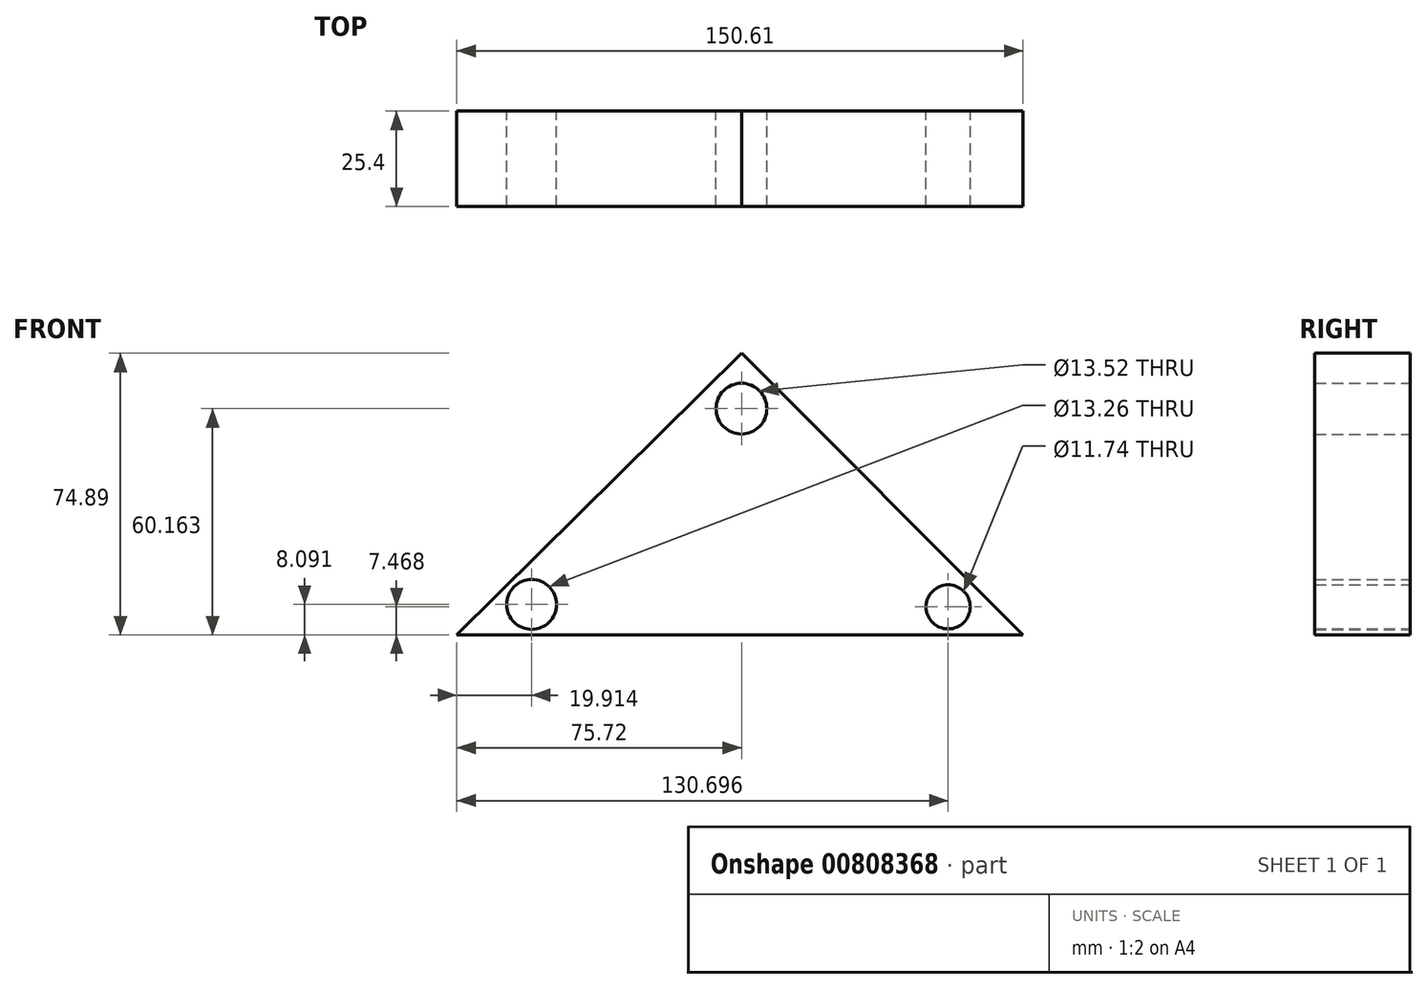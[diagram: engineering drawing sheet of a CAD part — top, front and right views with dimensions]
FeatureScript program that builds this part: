
annotation { "Feature Type Name" : "Feature", "Feature Type Description" : "" }
export const myFeature = defineFeature(function(context is Context, id is Id, definition is map)
    precondition{}
    {
        {
            var Q0;
            Q0=qCreatedBy(makeId("Front.planeOp"),FACE);
            var sketch = newSketch(context, id + "F0", { "sketchPlane" : qUnion([Q0])});
            skLineSegment(sketch, "E0", {"start": v(-75.72, 0) * mm, "end": v(74.9, 0) * mm});
            skLineSegment(sketch, "E1", {"start": v(74.9, 0) * mm, "end": v(0, 74.9) * mm});
            skLineSegment(sketch, "E2", {"start": v(0, 74.9) * mm, "end": v(-75.72, 0) * mm});
            skCircle(sketch, "E3", {"center": v(0, 60.16) * mm, "radius": 6.76 * mm});
            skCircle(sketch, "E4", {"center": v(-55.8, 8.1) * mm, "radius": 6.63 * mm});
            skCircle(sketch, "E5", {"center": v(54.98, 7.47) * mm, "radius": 5.87 * mm});
            skSolve(sketch);
        }
        {
            var Q0;
            Q0=makeQuery(id+"F0.imprint","IMPRINT",FACE,{"disambiguationData":[TD([[makeQuery(id+"F0.imprint","IMPRINT",EDGE,{"derivedFrom":sQuery(id+"F0.wireOp",EDGE,"E0")}),1.0]])]});
            extrude(context, id + "F1", {"entities" : qUnion([Q0]), "depth" : 25.4 * mm, "offsetDistance" : 25.4 * mm});
        }
    });
